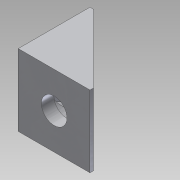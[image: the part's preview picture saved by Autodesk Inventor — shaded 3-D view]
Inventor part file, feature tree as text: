
AUTODESK INVENTOR PART (.ipt)
format: ipt  version: 2013 SP2 (Build 170200200, 200)  size: 122,880 bytes
history: native  units: mm
features: extrude x5, sketch x5, plane x1
ambient origin geometry x8: Origin, YZ Plane, XZ Plane, XY Plane, X Axis, Y Axis, Z Axis, Center Point
bodies: Solid1 (feature_tree)
feature tree (11):
  extrude  "Extrusion1"  Depth=20.0mm
  extrude  "Extrusion2"  Depth=26.87mm
  extrude  "Extrusion3"  Depth=20.0mm TaperAngle=0.0deg
  plane  "Work Plane1"
  extrude  "Extrusion4"  Depth=11.0mm
  extrude  "Extrusion5"  Depth=20.0mm TaperAngle=0.0deg
  sketch  "Sketch1"  dims[d0=20.0mm d1=20.0mm]
  sketch  "Sketch2"  dims[d2=1.0mm d3=26.87mm]
  sketch  "Sketch3"  dims[d4=1.000082mm d5=20.0mm d6=0.0mm]
  sketch  "Sketch4"  dims[d7=7.14mm d8=11.0mm]
  sketch  "Sketch5"  dims[d9=4.5mm d10=20.0mm d11=0.0mm d12=7.14mm d13=20.0mm d14=0.0mm d15=11.0mm d16=16.5mm d17=0.0mm d18=11.0mm d19=16.5mm d20=0.0mm]
